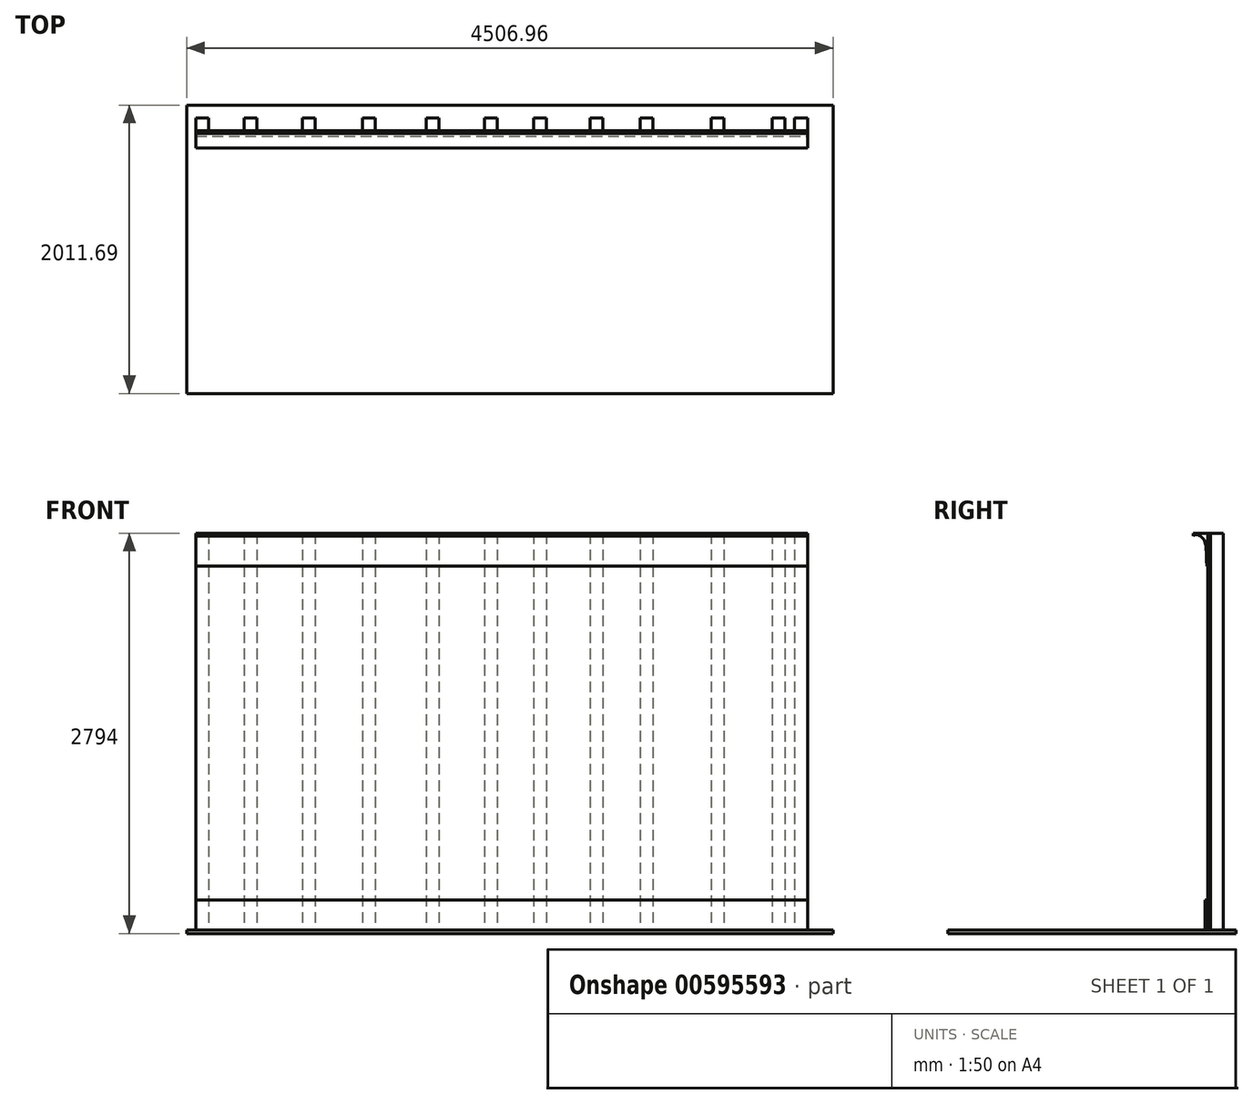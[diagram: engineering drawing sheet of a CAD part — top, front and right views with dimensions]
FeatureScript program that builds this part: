
annotation { "Feature Type Name" : "Feature", "Feature Type Description" : "" }
export const myFeature = defineFeature(function(context is Context, id is Id, definition is map)
    precondition{}
    {
        {
            var Q0;
            Q0=qCreatedBy(makeId("Front.planeOp"),FACE);
            var sketch = newSketch(context, id + "F0", { "sketchPlane" : qUnion([Q0])});
            skLineSegment(sketch, "E0.bottom", {"start": v(-2429.72, 0) * mm, "end": v(1837.48, 0) * mm});
            skLineSegment(sketch, "E0.top", {"start": v(-2429.72, 2768.6) * mm, "end": v(1837.48, 2768.6) * mm});
            skLineSegment(sketch, "E0.left", {"start": v(-2429.72, 0) * mm, "end": v(-2429.72, 2768.6) * mm});
            skLineSegment(sketch, "E0.right", {"start": v(1837.48, 0) * mm, "end": v(1837.48, 2768.6) * mm});
            skSolve(sketch);
        }
        {
            var Q0;
            Q0 = qSketchRegion(id + "F0", true);
            extrude(context, id + "F1", {"entities" : qUnion([Q0]), "oppositeDirection" : true, "depth" : 19.05 * mm, "offsetDistance" : 25.4 * mm});
        }
        {
            var Q0;
            Q0=makeQuery(id+"F1.opExtrude","CAP_FACE",FACE,{"disambiguationData":[OSD([sQuery(id+"F0.wireOp",EDGE,"E0.bottom"),sQuery(id+"F0.wireOp",EDGE,"E0.top"),sQuery(id+"F0.wireOp",EDGE,"E0.left"),sQuery(id+"F0.wireOp",EDGE,"E0.right")])],"isStart":false});
            var sketch = newSketch(context, id + "F2", { "sketchPlane" : qUnion([Q0])});
            skLineSegment(sketch, "E1.bottom", {"start": v(2429.72, 2768.6) * mm, "end": v(2340.82, 2768.6) * mm});
            skLineSegment(sketch, "E1.top", {"start": v(2429.72, 0) * mm, "end": v(2340.82, 0) * mm});
            skLineSegment(sketch, "E1.left", {"start": v(2429.72, 2768.6) * mm, "end": v(2429.72, 0) * mm});
            skLineSegment(sketch, "E1.right", {"start": v(2340.82, 2768.6) * mm, "end": v(2340.82, 0) * mm});
            skLineSegment(sketch, "E2.bottom", {"start": v(-1837.48, 2768.6) * mm, "end": v(-1744.74, 2768.6) * mm});
            skLineSegment(sketch, "E2.top", {"start": v(-1837.48, 0) * mm, "end": v(-1744.74, 0) * mm});
            skLineSegment(sketch, "E2.left", {"start": v(-1837.48, 2768.6) * mm, "end": v(-1837.48, 0) * mm});
            skLineSegment(sketch, "E2.right", {"start": v(-1744.74, 2768.6) * mm, "end": v(-1744.74, 0) * mm});
            skLineSegment(sketch, "E3.bottom", {"start": v(2093.17, 2768.6) * mm, "end": v(2004.27, 2768.6) * mm});
            skLineSegment(sketch, "E3.top", {"start": v(2093.17, 0) * mm, "end": v(2004.27, 0) * mm});
            skLineSegment(sketch, "E3.left", {"start": v(2093.17, 2768.6) * mm, "end": v(2093.17, 0) * mm});
            skLineSegment(sketch, "E3.right", {"start": v(2004.27, 2768.6) * mm, "end": v(2004.27, 0) * mm});
            skLineSegment(sketch, "E4.bottom", {"start": v(1686.77, 2768.6) * mm, "end": v(1597.87, 2768.6) * mm});
            skLineSegment(sketch, "E4.top", {"start": v(1686.77, 0) * mm, "end": v(1597.87, 0) * mm});
            skLineSegment(sketch, "E4.left", {"start": v(1686.77, 2768.6) * mm, "end": v(1686.77, 0) * mm});
            skLineSegment(sketch, "E4.right", {"start": v(1597.87, 2768.6) * mm, "end": v(1597.87, 0) * mm});
            skLineSegment(sketch, "E5.bottom", {"start": v(1267.67, 2768.6) * mm, "end": v(1178.77, 2768.6) * mm});
            skLineSegment(sketch, "E5.top", {"start": v(1267.67, 0) * mm, "end": v(1178.77, 0) * mm});
            skLineSegment(sketch, "E5.left", {"start": v(1267.67, 2768.6) * mm, "end": v(1267.67, 0) * mm});
            skLineSegment(sketch, "E5.right", {"start": v(1178.77, 2768.6) * mm, "end": v(1178.77, 0) * mm});
            skLineSegment(sketch, "E6", {"start": v(2385.27, 2768.6) * mm, "end": v(2385.27, 0) * mm, "construction": true});
            skLineSegment(sketch, "E7", {"start": v(2048.72, 0) * mm, "end": v(2048.72, 2768.6) * mm, "construction": true});
            skLineSegment(sketch, "E8", {"start": v(1642.32, 2768.6) * mm, "end": v(1642.32, 0) * mm, "construction": true});
            skLineSegment(sketch, "E9", {"start": v(1223.22, 0) * mm, "end": v(1223.22, 2768.6) * mm, "construction": true});
            skLineSegment(sketch, "E10.bottom", {"start": v(823.17, 2768.6) * mm, "end": v(734.27, 2768.6) * mm});
            skLineSegment(sketch, "E10.top", {"start": v(823.17, 0) * mm, "end": v(734.27, 0) * mm});
            skLineSegment(sketch, "E10.left", {"start": v(823.17, 2768.6) * mm, "end": v(823.17, 0) * mm});
            skLineSegment(sketch, "E10.right", {"start": v(734.27, 2768.6) * mm, "end": v(734.27, 0) * mm});
            skLineSegment(sketch, "E11", {"start": v(778.72, 0) * mm, "end": v(778.72, 2768.6) * mm, "construction": true});
            skLineSegment(sketch, "E12.bottom", {"start": v(416.77, 2768.6) * mm, "end": v(327.87, 2768.6) * mm});
            skLineSegment(sketch, "E12.top", {"start": v(416.77, 0) * mm, "end": v(327.87, 0) * mm});
            skLineSegment(sketch, "E12.left", {"start": v(416.77, 2768.6) * mm, "end": v(416.77, 0) * mm});
            skLineSegment(sketch, "E12.right", {"start": v(327.87, 2768.6) * mm, "end": v(327.87, 0) * mm});
            skLineSegment(sketch, "E13", {"start": v(372.32, 0) * mm, "end": v(372.32, 2768.6) * mm, "construction": true});
            skLineSegment(sketch, "E14.bottom", {"start": v(73.87, 2768.6) * mm, "end": v(-15.03, 2768.6) * mm});
            skLineSegment(sketch, "E14.top", {"start": v(73.87, 0) * mm, "end": v(-15.03, 0) * mm});
            skLineSegment(sketch, "E14.left", {"start": v(73.87, 2768.6) * mm, "end": v(73.87, 0) * mm});
            skLineSegment(sketch, "E14.right", {"start": v(-15.03, 2768.6) * mm, "end": v(-15.03, 0) * mm});
            skLineSegment(sketch, "E15", {"start": v(29.42, 0) * mm, "end": v(29.42, 2768.6) * mm, "construction": true});
            skLineSegment(sketch, "E16.bottom", {"start": v(-319.83, 2768.6) * mm, "end": v(-408.73, 2768.6) * mm});
            skLineSegment(sketch, "E16.top", {"start": v(-319.83, 0) * mm, "end": v(-408.73, 0) * mm});
            skLineSegment(sketch, "E16.left", {"start": v(-319.83, 2768.6) * mm, "end": v(-319.83, 0) * mm});
            skLineSegment(sketch, "E16.right", {"start": v(-408.73, 2768.6) * mm, "end": v(-408.73, 0) * mm});
            skLineSegment(sketch, "E17", {"start": v(-364.28, 0) * mm, "end": v(-364.28, 2768.6) * mm, "construction": true});
            skLineSegment(sketch, "E18.bottom", {"start": v(-669.08, 2768.6) * mm, "end": v(-757.98, 2768.6) * mm});
            skLineSegment(sketch, "E18.top", {"start": v(-669.08, 0) * mm, "end": v(-757.98, 0) * mm});
            skLineSegment(sketch, "E18.left", {"start": v(-669.08, 2768.6) * mm, "end": v(-669.08, 0) * mm});
            skLineSegment(sketch, "E18.right", {"start": v(-757.98, 2768.6) * mm, "end": v(-757.98, 0) * mm});
            skLineSegment(sketch, "E19", {"start": v(-713.53, 0) * mm, "end": v(-713.53, 2768.6) * mm, "construction": true});
            skLineSegment(sketch, "E20.bottom", {"start": v(-1164.38, 2768.6) * mm, "end": v(-1253.28, 2768.6) * mm});
            skLineSegment(sketch, "E20.top", {"start": v(-1164.38, 0) * mm, "end": v(-1253.28, 0) * mm});
            skLineSegment(sketch, "E20.left", {"start": v(-1164.38, 2768.6) * mm, "end": v(-1164.38, 0) * mm});
            skLineSegment(sketch, "E20.right", {"start": v(-1253.28, 2768.6) * mm, "end": v(-1253.28, 0) * mm});
            skLineSegment(sketch, "E21", {"start": v(-1208.83, 0) * mm, "end": v(-1208.83, 2768.6) * mm, "construction": true});
            skLineSegment(sketch, "E22.bottom", {"start": v(-1589.83, 2768.6) * mm, "end": v(-1678.73, 2768.6) * mm});
            skLineSegment(sketch, "E22.top", {"start": v(-1589.83, 0) * mm, "end": v(-1678.73, 0) * mm});
            skLineSegment(sketch, "E22.left", {"start": v(-1589.83, 2768.6) * mm, "end": v(-1589.83, 0) * mm});
            skLineSegment(sketch, "E22.right", {"start": v(-1678.73, 2768.6) * mm, "end": v(-1678.73, 0) * mm});
            skLineSegment(sketch, "E23", {"start": v(-1634.28, 0) * mm, "end": v(-1634.28, 2768.6) * mm, "construction": true});
            skSolve(sketch);
        }
        {
            var Q0;
            Q0 = qSketchRegion(id + "F2", true);
            extrude(context, id + "F3", {"entities" : qUnion([Q0]), "depth" : 88.9 * mm, "offsetDistance" : 25.4 * mm});
        }
        {
            var Q0;
            Q0=makeQuery(id+"F1.opExtrude","CAP_FACE",FACE,{"disambiguationData":[OSD([sQuery(id+"F0.wireOp",EDGE,"E0.bottom"),sQuery(id+"F0.wireOp",EDGE,"E0.top"),sQuery(id+"F0.wireOp",EDGE,"E0.left"),sQuery(id+"F0.wireOp",EDGE,"E0.right")])],"isStart":true});
            var sketch = newSketch(context, id + "F4", { "sketchPlane" : qUnion([Q0])});
            skLineSegment(sketch, "E24.bottom", {"start": v(-2429.72, 0) * mm, "end": v(1837.48, 0) * mm});
            skLineSegment(sketch, "E24.top", {"start": v(-2429.72, 209.55) * mm, "end": v(1837.48, 209.55) * mm});
            skLineSegment(sketch, "E24.left", {"start": v(-2429.72, 0) * mm, "end": v(-2429.72, 209.55) * mm});
            skLineSegment(sketch, "E24.right", {"start": v(1837.48, 0) * mm, "end": v(1837.48, 209.55) * mm});
            skSolve(sketch);
        }
        {
            var Q0;
            Q0 = qSketchRegion(id + "F4", true);
            extrude(context, id + "F5", {"entities" : qUnion([Q0]), "depth" : 19.05 * mm, "offsetDistance" : 25.4 * mm});
        }
        {
            var Q0;
            Q0=makeQuery(id+"F3.opExtrude","SWEPT_FACE",FACE,{"disambiguationData":[OSD([sQuery(id+"F2.wireOp",EDGE,"E1.left")])]});
            var sketch = newSketch(context, id + "F6", { "sketchPlane" : qUnion([Q0])});
            skLineSegment(sketch, "E25", {"start": v(0, 2768.6) * mm, "end": v(101.6, 2768.6) * mm});
            skLineSegment(sketch, "E26", {"start": v(0, 2540) * mm, "end": v(0, 2768.6) * mm});
            skLineSegment(sketch, "E27", {"start": v(0, 2540) * mm, "end": v(6.35, 2540) * mm});
            skLineSegment(sketch, "E28", {"start": v(101.6, 2768.6) * mm, "end": v(101.6, 2749.55) * mm});
            skFitSpline(sketch, "E29", {"points": [v(101.6, 2749.55) * mm, v(66.13, 2755.9) * mm, v(23.04, 2715.56) * mm, v(11.44, 2643.51) * mm, v(6.35, 2540) * mm], "startDerivative": vector(-162.25, 161.24) * mm, "endDerivative": vector(-26.8, -312.04) * mm});
            skSolve(sketch);
        }
        {
            var Q0;
            Q0 = qSketchRegion(id + "F6", true);
            var Q1;
            Q1=makeQuery(id+"F3.opExtrude","SWEPT_FACE",FACE,{"disambiguationData":[OSD([sQuery(id+"F2.wireOp",EDGE,"E2.left")])]});
            extrude(context, id + "F7", {"entities" : qUnion([Q0]), "endBound" : BoundingType.UP_TO_SURFACE, "oppositeDirection" : true, "depth" : 25.4 * mm, "endBoundEntityFace" : qUnion([Q1]), "offsetDistance" : 25.4 * mm});
        }
        {
            var Q0;
            Q0=qCreatedBy(makeId("Top.planeOp"),FACE);
            var sketch = newSketch(context, id + "F8", { "sketchPlane" : qUnion([Q0])});
            skLineSegment(sketch, "E30.bottom", {"start": v(-2493.19, 197.26) * mm, "end": v(2013.77, 197.26) * mm});
            skLineSegment(sketch, "E30.top", {"start": v(-2493.19, -1814.43) * mm, "end": v(2013.77, -1814.43) * mm});
            skLineSegment(sketch, "E30.left", {"start": v(-2493.19, 197.26) * mm, "end": v(-2493.19, -1814.43) * mm});
            skLineSegment(sketch, "E30.right", {"start": v(2013.77, 197.26) * mm, "end": v(2013.77, -1814.43) * mm});
            skSolve(sketch);
        }
        {
            var Q0;
            Q0 = qSketchRegion(id + "F8", true);
            extrude(context, id + "F9", {"entities" : qUnion([Q0]), "oppositeDirection" : true, "depth" : 25.4 * mm, "offsetDistance" : 25.4 * mm});
        }
    });
